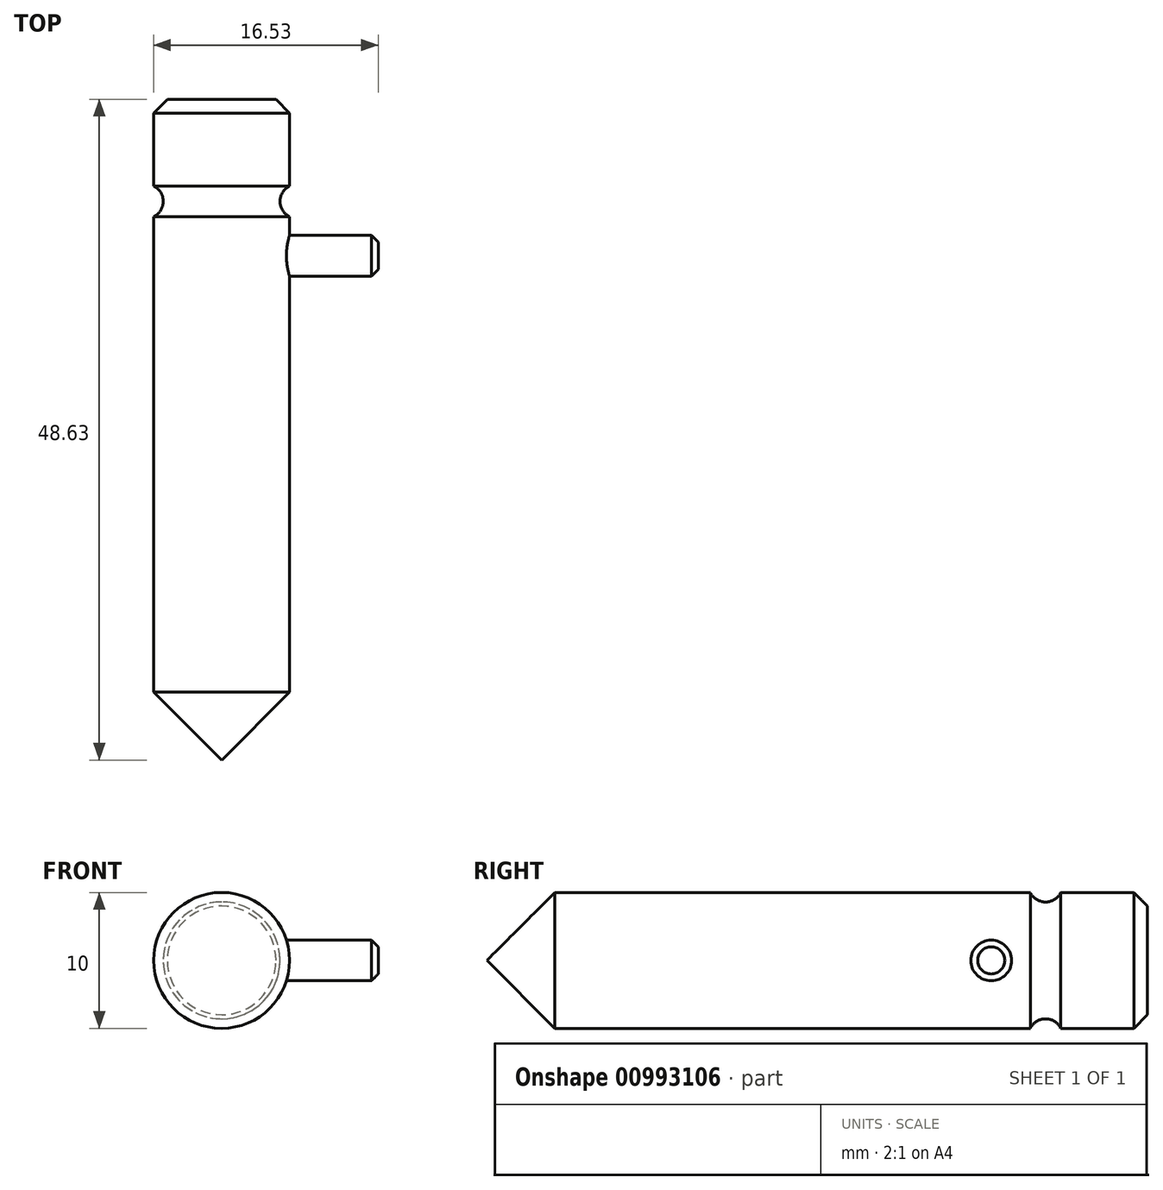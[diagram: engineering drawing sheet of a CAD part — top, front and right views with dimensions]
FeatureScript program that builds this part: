
annotation { "Feature Type Name" : "Feature", "Feature Type Description" : "" }
export const myFeature = defineFeature(function(context is Context, id is Id, definition is map)
    precondition{}
    {
        {
            var Q0;
            Q0=qCreatedBy(makeId("Front.planeOp"),FACE);
            var sketch = newSketch(context, id + "F0", { "sketchPlane" : qUnion([Q0])});
            skCircle(sketch, "E0", {"center": v(0, 0) * mm, "radius": 5 * mm});
            skSolve(sketch);
        }
        {
            var Q0;
            Q0=qSketchRegion(id+"F0",true);
            extrude(context, id + "F1", {"entities" : qUnion([Q0]), "depth" : 40 * mm});
        }
        {
            var Q0;
            Q0=makeQuery(id+"F1.opExtrude","CAP_FACE",FACE,{"disambiguationData":[OSD([sQuery(id+"F0.wireOp",EDGE,"E0")])],"isStart":true});
            var sketch = newSketch(context, id + "F2", { "sketchPlane" : qUnion([Q0])});
            skCircle(sketch, "E1", {"center": v(0, 0) * mm, "radius": 4.3 * mm});
            skSolve(sketch);
        }
        {
            var Q0;
            Q0=qSketchRegion(id+"F2",true);
            extrude(context, id + "F3", {"entities" : qUnion([Q0]), "operationType" : NewBodyOperationType.ADD, "depth" : 2.25 * mm});
        }
        {
            var Q0;
            Q0=makeQuery(id+"F3.opExtrude","CAP_FACE",FACE,{"disambiguationData":[OSD([sQuery(id+"F2.wireOp",EDGE,"E1")])],"isStart":false});
            var sketch = newSketch(context, id + "F4", { "sketchPlane" : qUnion([Q0])});
            skCircle(sketch, "E2", {"center": v(0, 0) * mm, "radius": 5 * mm});
            skSolve(sketch);
        }
        {
            var Q0;
            Q0=qSketchRegion(id+"F4",true);
            extrude(context, id + "F5", {"entities" : qUnion([Q0]), "operationType" : NewBodyOperationType.ADD, "depth" : 6.38 * mm});
        }
        {
            var Q0;
            Q0=makeQuery(id+"F3.opExtrude","SWEPT_FACE",FACE,{"disambiguationData":[OSD([sQuery(id+"F2.wireOp",EDGE,"E1")])]});
            fillet(context, id + "F6", {"entities" : qUnion([Q0]), "radius" : 1.25 * mm, "tangentPropagation" : true, "allowEdgeOverflow" : false});
        }
        {
            var Q0;
            Q0=makeQuery(id+"F5.opExtrude","CAP_EDGE",EDGE,{"disambiguationData":[OSD([sQuery(id+"F4.wireOp",EDGE,"E2")])],"isStart":false});
            chamfer(context, id + "F7", {"entities" : qUnion([Q0]), "width" : 1 * mm, "tangentPropagation" : true});
        }
        {
            var Q0;
            Q0=qCreatedBy(makeId("Right.planeOp"),FACE);
            var sketch = newSketch(context, id + "F8", { "sketchPlane" : qUnion([Q0])});
            skCircle(sketch, "E3", {"center": v(-2.87, 0) * mm, "radius": 1.5 * mm});
            skSolve(sketch);
        }
        {
            var Q0;
            Q0=qSketchRegion(id+"F8",true);
            extrude(context, id + "F9", {"entities" : qUnion([Q0]), "operationType" : NewBodyOperationType.ADD, "depth" : 11.53 * mm});
        }
        {
            var Q0;
            Q0=makeQuery(id+"F9.opExtrude","CAP_EDGE",EDGE,{"disambiguationData":[OSD([sQuery(id+"F8.wireOp",EDGE,"E3")])],"isStart":false});
            chamfer(context, id + "F10", {"entities" : qUnion([Q0]), "width" : 0.5 * mm, "tangentPropagation" : true});
        }
        {
            var Q0;
            Q0=makeQuery(id+"F1.opExtrude","CAP_EDGE",EDGE,{"disambiguationData":[OSD([sQuery(id+"F0.wireOp",EDGE,"E0")])],"isStart":false});
            chamfer(context, id + "F11", {"entities" : qUnion([Q0]), "width" : 5 * mm, "tangentPropagation" : true});
        }
    });
